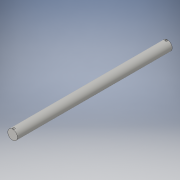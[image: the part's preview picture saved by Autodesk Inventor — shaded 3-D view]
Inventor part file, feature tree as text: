
AUTODESK INVENTOR PART (.ipt)
format: ipt  version: 2016 (Build 200138000, 138)  size: 104,960 bytes
history: native  units: in
note: dims shown in document units (in); Inventor stores cm internally (conversion verified against a paired STEP export)
features: extrude x2, sketch x2
ambient origin geometry x8: Origin, YZ Plane, XZ Plane, XY Plane, X Axis, Y Axis, Z Axis, Center Point
bodies: Solid1 (feature_tree)
feature tree (4):
  extrude  "Extrusion1"  Depth=8.0in TaperAngle=0.0deg
  extrude  "Extrusion4"  Depth=0.06in
  sketch  "Sketch1"  dims[d0=0.5in d1=8.0in d2=0.0in]
  sketch  "Sketch4"  dims[d13=0.06in d15=0.06in d16=0.1in d17=0.6in d18=0.0in d19=0.1in]
